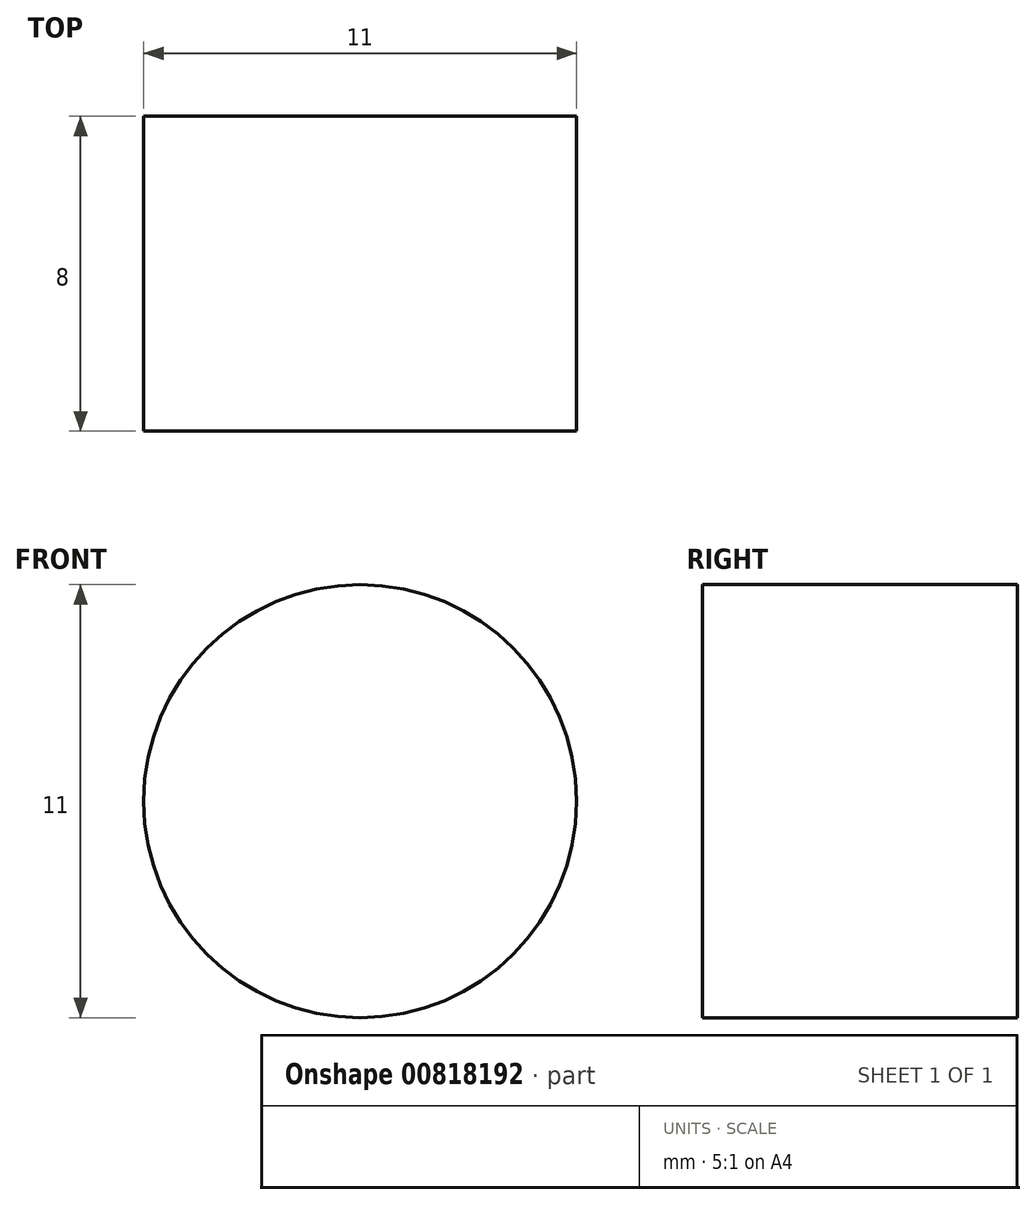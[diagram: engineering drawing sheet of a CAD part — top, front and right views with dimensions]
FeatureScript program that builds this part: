
annotation { "Feature Type Name" : "Feature", "Feature Type Description" : "" }
export const myFeature = defineFeature(function(context is Context, id is Id, definition is map)
    precondition{}
    {
        {
            var Q0;
            Q0=qCreatedBy(makeId("Front.planeOp"),FACE);
            var sketch = newSketch(context, id + "F0", { "sketchPlane" : qUnion([Q0])});
            skCircle(sketch, "E0", {"center": v(0, 0) * mm, "radius": 27.25 * mm});
            skCircle(sketch, "E1", {"center": v(48.5, 0) * mm, "radius": 5.5 * mm});
            skCircle(sketch, "E2", {"center": v(-48.5, 0) * mm, "radius": 5.5 * mm});
            skArc(sketch, "E3", {"start": v(-56.99, -10.5) * mm, "mid": v(-62, 0) * mm, "end": v(-56.99, 10.5) * mm});
            skArc(sketch, "E4", {"start": v(-27.67, 34.21) * mm, "mid": v(0, 44) * mm, "end": v(27.67, 34.21) * mm});
            skArc(sketch, "E5", {"start": v(56.99, 10.5) * mm, "mid": v(62, 0) * mm, "end": v(56.99, -10.5) * mm});
            skArc(sketch, "E6", {"start": v(27.67, -34.21) * mm, "mid": v(0, -44) * mm, "end": v(-27.67, -34.21) * mm});
            skLineSegment(sketch, "E7", {"start": v(-56.99, 10.5) * mm, "end": v(-27.67, 34.21) * mm});
            skLineSegment(sketch, "E8", {"start": v(27.67, 34.21) * mm, "end": v(56.99, 10.5) * mm});
            skLineSegment(sketch, "E9", {"start": v(56.99, -10.5) * mm, "end": v(27.67, -34.21) * mm});
            skLineSegment(sketch, "E10", {"start": v(-27.67, -34.21) * mm, "end": v(-56.99, -10.5) * mm});
            skSolve(sketch);
        }
        {
            var Q0;
            Q0=makeQuery(id+"F0.imprint","IMPRINT",FACE,{"disambiguationData":[TD([[makeQuery(id+"F0.imprint","IMPRINT",EDGE,{"derivedFrom":sQuery(id+"F0.wireOp",EDGE,"E1")}),1.0]])]});
            extrude(context, id + "F1", {"entities" : qUnion([Q0]), "depth" : 8 * mm, "offsetDistance" : 25 * mm});
        }
    });
